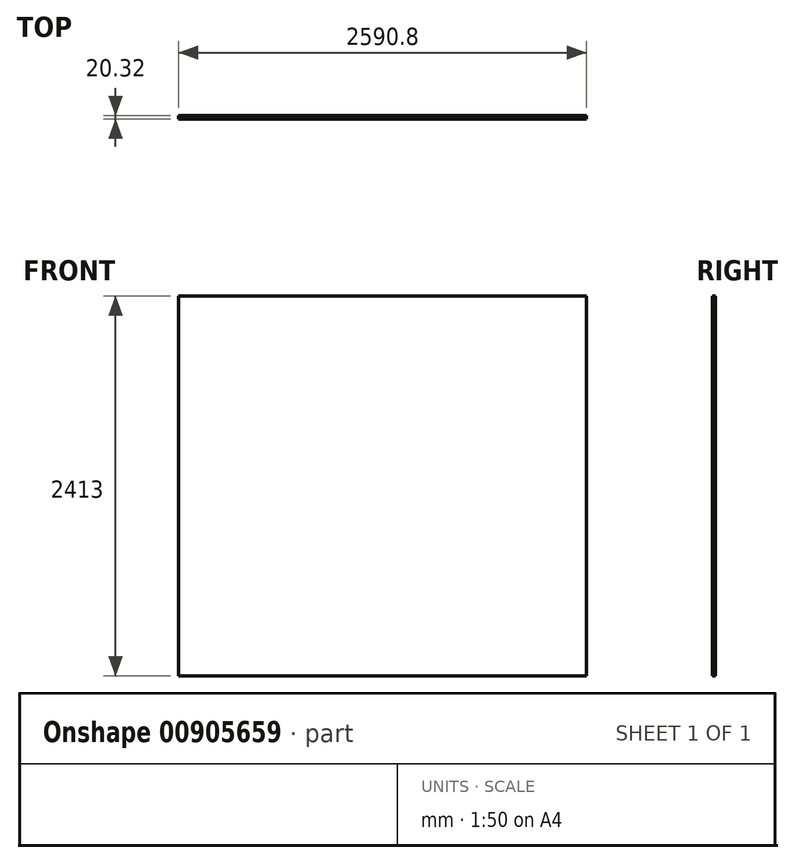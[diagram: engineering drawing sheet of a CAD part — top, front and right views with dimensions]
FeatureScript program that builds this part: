
annotation { "Feature Type Name" : "Feature", "Feature Type Description" : "" }
export const myFeature = defineFeature(function(context is Context, id is Id, definition is map)
    precondition{}
    {
        {
            var Q0;
            Q0=qCreatedBy(makeId("Front.planeOp"),FACE);
            var sketch = newSketch(context, id + "F0", { "sketchPlane" : qUnion([Q0])});
            skLineSegment(sketch, "E0.bottom", {"start": v(-1295.4, 1206.5) * mm, "end": v(1295.4, 1206.5) * mm});
            skLineSegment(sketch, "E0.top", {"start": v(-1295.4, -1206.5) * mm, "end": v(1295.4, -1206.5) * mm});
            skLineSegment(sketch, "E0.left", {"start": v(-1295.4, 1206.5) * mm, "end": v(-1295.4, -1206.5) * mm});
            skLineSegment(sketch, "E0.right", {"start": v(1295.4, 1206.5) * mm, "end": v(1295.4, -1206.5) * mm});
            skPoint(sketch, "E0.middle", {"position": v(0, 0) * mm});
            skSolve(sketch);
        }
        {
            var Q0;
            Q0=makeQuery(id+"F0.imprint","IMPRINT",FACE,{"disambiguationData":[TD([[makeQuery(id+"F0.imprint","IMPRINT",EDGE,{"derivedFrom":sQuery(id+"F0.wireOp",EDGE,"E0.bottom")}),-1.0]])]});
            extrude(context, id + "F1", {"entities" : qUnion([Q0]), "depth" : 20.32 * mm, "offsetDistance" : 25.4 * mm});
        }
    });
